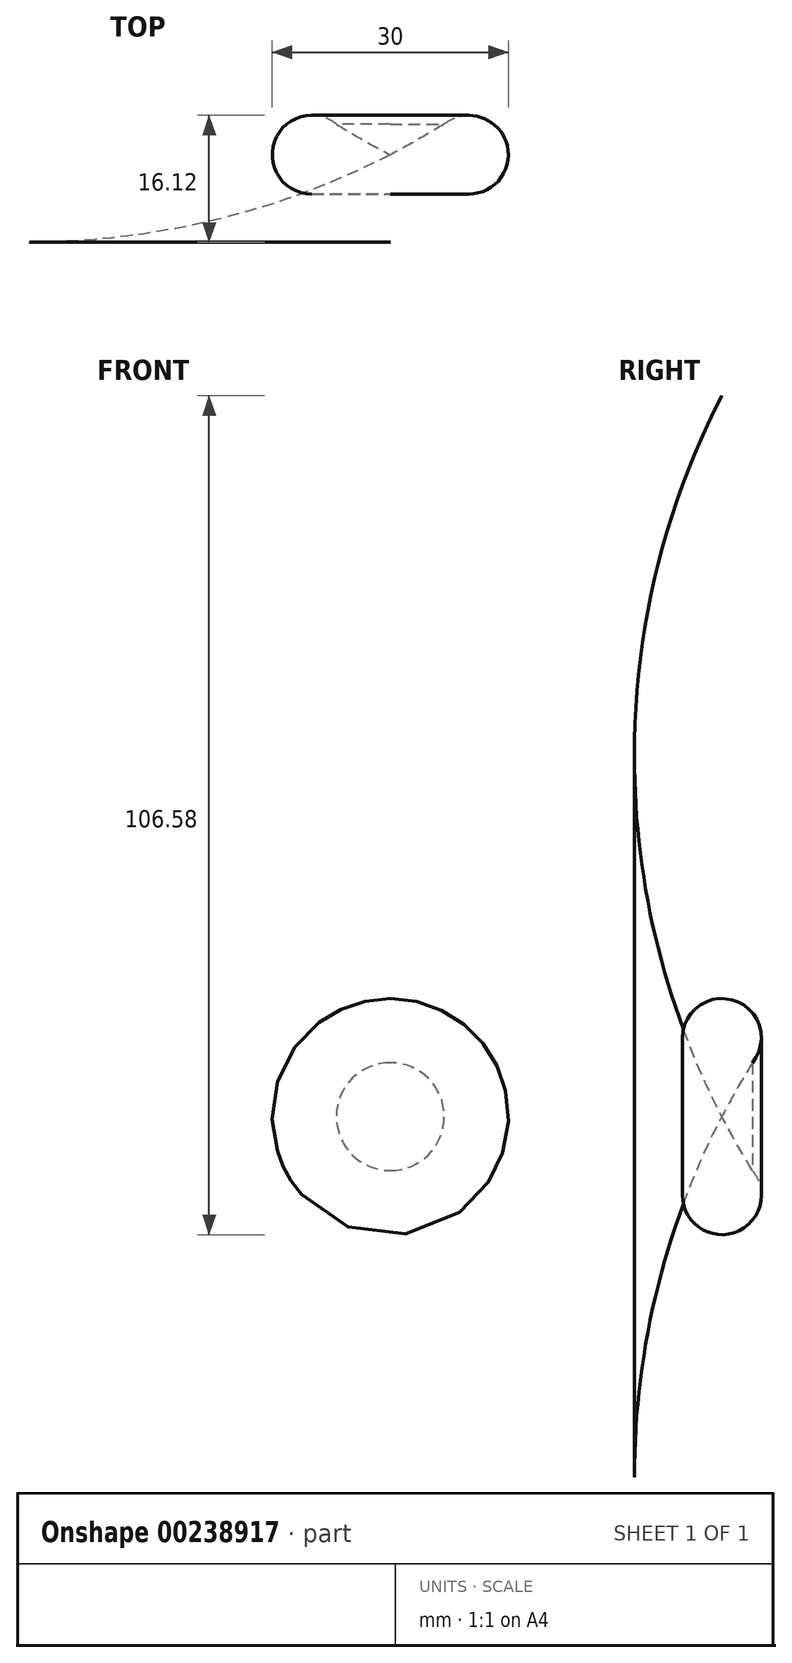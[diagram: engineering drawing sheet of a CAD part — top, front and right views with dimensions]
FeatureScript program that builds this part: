
annotation { "Feature Type Name" : "Feature", "Feature Type Description" : "" }
export const myFeature = defineFeature(function(context is Context, id is Id, definition is map)
    precondition{}
    {
        {
            var Q0;
            Q0=qCreatedBy(makeId("Top.planeOp"),FACE);
            var sketch = newSketch(context, id + "F0", { "sketchPlane" : qUnion([Q0])});
            skCircle(sketch, "E0", {"center": v(0, 0) * mm, "radius": 5 * mm});
            skLineSegment(sketch, "E1", {"start": v(10, 0) * mm, "end": v(10, -5) * mm});
            skLineSegment(sketch, "E2", {"start": v(10, -5) * mm, "end": v(0, -5) * mm});
            skArc(sketch, "E3", {"start": v(3.15, 3.88) * mm, "mid": v(6.54, 1.87) * mm, "end": v(10, 0) * mm});
            skSolve(sketch);
        }
        {
            var Q0;
            {var subQ0=sQuery(id+"F0.wireOp",EDGE,"E0");var subQ1=makeQuery(id+"F0.imprint","INTERSECT",VERTEX,{"derivedFrom":[subQ0,sQuery(id+"F0.wireOp",EDGE,"E2")]});Q0=makeQuery(id+"F0.imprint","IMPRINT",FACE,{"disambiguationData":[TD([[makeQuery(id+"F0.imprint","IMPRINT",EDGE,{"disambiguationData":[TD([[subQ1,1.0]])],"derivedFrom":subQ0}),1.0]])]});}
            var Q1;
            Q1=makeQuery(id+"F0.imprint","IMPRINT",FACE,{"disambiguationData":[TD([[makeQuery(id+"F0.imprint","IMPRINT",EDGE,{"derivedFrom":sQuery(id+"F0.wireOp",EDGE,"E1")}),-1.0]])]});
            var Q2;
            Q2=sQuery(id+"F0.wireOp",EDGE,"E1");
            revolve(context, id + "F1", {"entities" : qUnion([Q0, Q1]), "axis" : qUnion([Q2]), "revolveType" : RevolveType.FULL});
        }
    });
